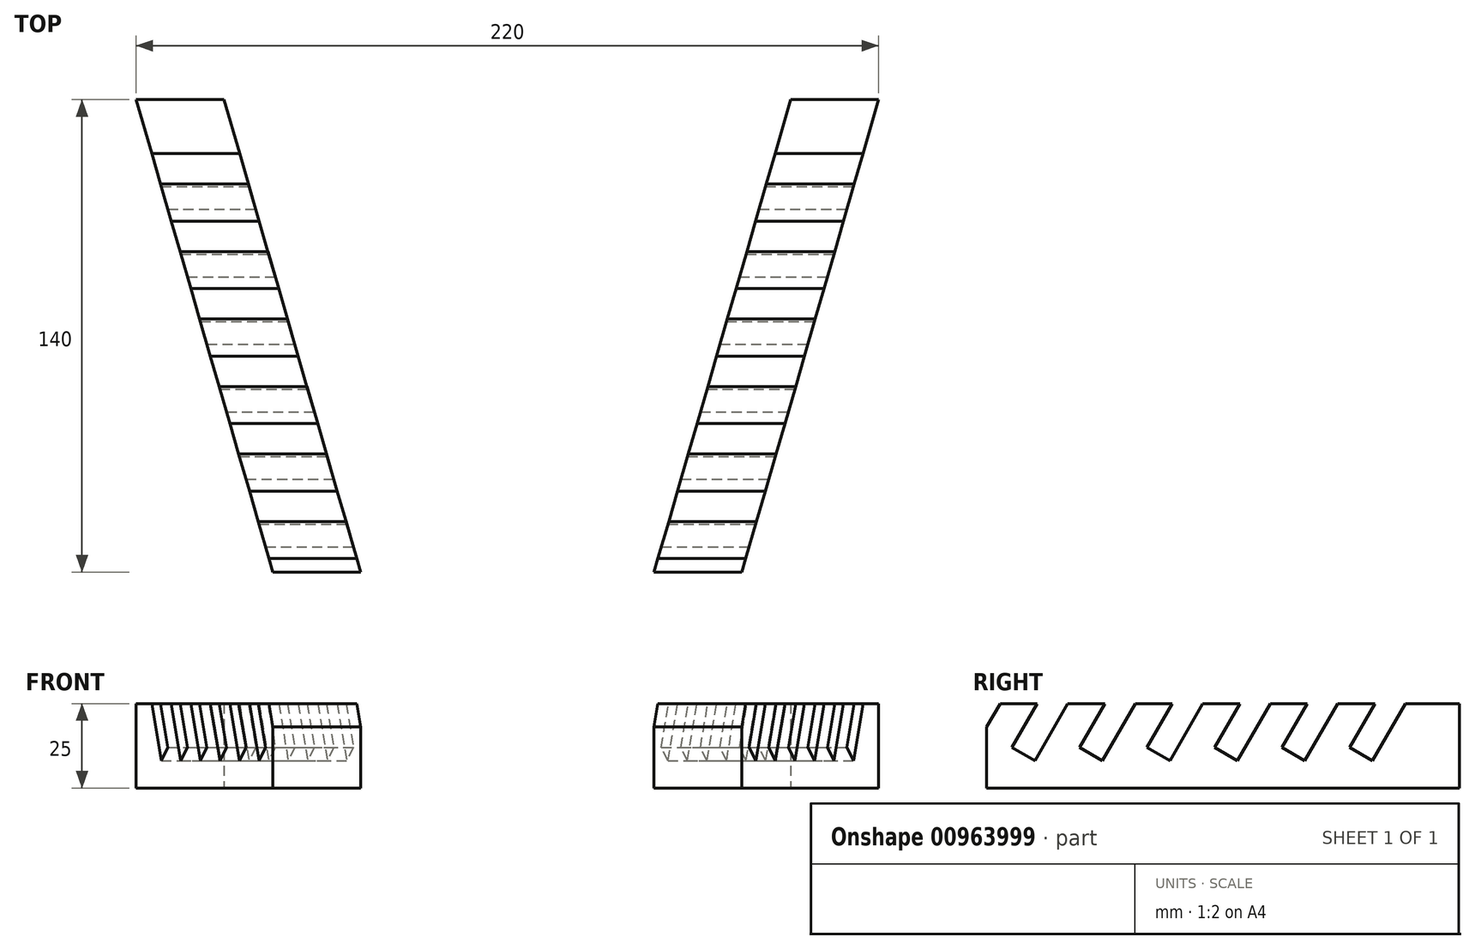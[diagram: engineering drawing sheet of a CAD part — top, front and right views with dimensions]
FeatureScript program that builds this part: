
annotation { "Feature Type Name" : "Feature", "Feature Type Description" : "" }
export const myFeature = defineFeature(function(context is Context, id is Id, definition is map)
    precondition{}
    {
        {
            var Q0;
            Q0=qCreatedBy(makeId("Top.planeOp"),FACE);
            var sketch = newSketch(context, id + "F0", { "sketchPlane" : qUnion([Q0])});
            skLineSegment(sketch, "E0", {"start": v(0, 0) * mm, "end": v(0, 380) * mm, "construction": true});
            skLineSegment(sketch, "E1", {"start": v(-110, 380) * mm, "end": v(-83.97, 380) * mm});
            skLineSegment(sketch, "E2", {"start": v(-110, 380) * mm, "end": v(0, 0) * mm});
            skLineSegment(sketch, "E3", {"start": v(110, 380) * mm, "end": v(0, 0) * mm});
            skLineSegment(sketch, "E4.0", {"start": v(-76.74, 355) * mm, "end": v(0, 89.9) * mm});
            skLineSegment(sketch, "E4.2", {"start": v(76.74, 355) * mm, "end": v(0, 89.9) * mm});
            skLineSegment(sketch, "E5", {"start": v(-76.74, 355) * mm, "end": v(-83.97, 380) * mm});
            skLineSegment(sketch, "E6", {"start": v(76.74, 355) * mm, "end": v(83.97, 380) * mm});
            skLineSegment(sketch, "E7.trimOffspring", {"start": v(83.97, 380) * mm, "end": v(110, 380) * mm});
            skSolve(sketch);
        }
        {
            var Q0;
            Q0=makeQuery(id+"F0.imprint","IMPRINT",FACE,{"disambiguationData":[TD([[makeQuery(id+"F0.imprint","IMPRINT",EDGE,{"derivedFrom":sQuery(id+"F0.wireOp",EDGE,"E1")}),-1.0]])]});
            extrude(context, id + "F1", {"entities" : qUnion([Q0]), "depth" : 25 * mm, "offsetDistance" : 25 * mm});
        }
        {
            var Q0;
            Q0=qCreatedBy(makeId("Right.planeOp"),FACE);
            var sketch = newSketch(context, id + "F2", { "sketchPlane" : qUnion([Q0])});
            skLineSegment(sketch, "E8", {"start": v(0, 0) * mm, "end": v(380, 0) * mm, "construction": true});
            skLineSegment(sketch, "E9", {"start": v(15, 0) * mm, "end": v(15, 35) * mm, "construction": true});
            skLineSegment(sketch, "E10", {"start": v(24, 0) * mm, "end": v(24, 35) * mm, "construction": true});
            skLineSegment(sketch, "E11", {"start": v(35, 0) * mm, "end": v(35, 35) * mm, "construction": true});
            skLineSegment(sketch, "E12", {"start": v(44, 0) * mm, "end": v(44, 35) * mm, "construction": true});
            skLineSegment(sketch, "E13", {"start": v(0, 0) * mm, "end": v(0, 25) * mm, "construction": true});
            skLineSegment(sketch, "E14", {"start": v(45.46, -18.54) * mm, "end": v(100.8, -18.54) * mm, "construction": true});
            skLineSegment(sketch, "E15", {"start": v(15, 25) * mm, "end": v(7.5, 12) * mm});
            skLineSegment(sketch, "E16", {"start": v(7.5, 12) * mm, "end": v(14.25, 8.11) * mm});
            skLineSegment(sketch, "E17", {"start": v(24, 25) * mm, "end": v(14.25, 8.11) * mm});
            skLineSegment(sketch, "E18", {"start": v(35, 25) * mm, "end": v(27.5, 12.01) * mm});
            skLineSegment(sketch, "E19", {"start": v(27.5, 12.01) * mm, "end": v(34.25, 8.11) * mm});
            skLineSegment(sketch, "E20", {"start": v(44, 25) * mm, "end": v(34.25, 8.11) * mm});
            skLineSegment(sketch, "E21", {"start": v(15, 25) * mm, "end": v(24, 25) * mm});
            skLineSegment(sketch, "E22", {"start": v(35, 25) * mm, "end": v(44, 25) * mm});
            skLineSegment(sketch, "E23", {"start": v(55, 25) * mm, "end": v(47.5, 12) * mm});
            skLineSegment(sketch, "E24", {"start": v(47.5, 12) * mm, "end": v(54.25, 8.11) * mm});
            skLineSegment(sketch, "E25", {"start": v(64, 25) * mm, "end": v(54.25, 8.11) * mm});
            skLineSegment(sketch, "E26", {"start": v(75, 25) * mm, "end": v(67.5, 12.01) * mm});
            skLineSegment(sketch, "E27", {"start": v(67.5, 12.01) * mm, "end": v(74.25, 8.11) * mm});
            skLineSegment(sketch, "E28", {"start": v(84, 25) * mm, "end": v(74.25, 8.11) * mm});
            skLineSegment(sketch, "E29", {"start": v(55, 25) * mm, "end": v(64, 25) * mm});
            skLineSegment(sketch, "E30", {"start": v(75, 25) * mm, "end": v(84, 25) * mm});
            skLineSegment(sketch, "E31", {"start": v(95, 25) * mm, "end": v(87.5, 12.01) * mm});
            skLineSegment(sketch, "E32", {"start": v(87.5, 12.01) * mm, "end": v(94.25, 8.11) * mm});
            skLineSegment(sketch, "E33", {"start": v(104, 25) * mm, "end": v(94.25, 8.11) * mm});
            skLineSegment(sketch, "E34", {"start": v(115, 25) * mm, "end": v(107.5, 12.01) * mm});
            skLineSegment(sketch, "E35", {"start": v(107.5, 12.01) * mm, "end": v(114.25, 8.11) * mm});
            skLineSegment(sketch, "E36", {"start": v(124, 25) * mm, "end": v(114.25, 8.11) * mm});
            skLineSegment(sketch, "E37", {"start": v(95, 25) * mm, "end": v(104, 25) * mm});
            skLineSegment(sketch, "E38", {"start": v(115, 25) * mm, "end": v(124, 25) * mm});
            skLineSegment(sketch, "E39", {"start": v(135, 25) * mm, "end": v(127.5, 12.01) * mm});
            skLineSegment(sketch, "E40", {"start": v(127.5, 12.01) * mm, "end": v(134.25, 8.11) * mm});
            skLineSegment(sketch, "E41", {"start": v(144, 25) * mm, "end": v(134.25, 8.11) * mm});
            skLineSegment(sketch, "E42", {"start": v(155, 25) * mm, "end": v(147.5, 12.01) * mm});
            skLineSegment(sketch, "E43", {"start": v(147.5, 12.01) * mm, "end": v(154.25, 8.11) * mm});
            skLineSegment(sketch, "E44", {"start": v(164, 25) * mm, "end": v(154.25, 8.11) * mm});
            skLineSegment(sketch, "E45", {"start": v(135, 25) * mm, "end": v(144, 25) * mm});
            skLineSegment(sketch, "E46", {"start": v(155, 25) * mm, "end": v(164, 25) * mm});
            skLineSegment(sketch, "E47", {"start": v(175, 25) * mm, "end": v(167.5, 12.01) * mm});
            skLineSegment(sketch, "E48", {"start": v(167.5, 12.01) * mm, "end": v(174.25, 8.11) * mm});
            skLineSegment(sketch, "E49", {"start": v(184, 25) * mm, "end": v(174.25, 8.11) * mm});
            skLineSegment(sketch, "E50", {"start": v(195, 25) * mm, "end": v(187.5, 12.01) * mm});
            skLineSegment(sketch, "E51", {"start": v(187.5, 12.01) * mm, "end": v(194.25, 8.11) * mm});
            skLineSegment(sketch, "E52", {"start": v(204, 25) * mm, "end": v(194.25, 8.11) * mm});
            skLineSegment(sketch, "E53", {"start": v(175, 25) * mm, "end": v(184, 25) * mm});
            skLineSegment(sketch, "E54", {"start": v(195, 25) * mm, "end": v(204, 25) * mm});
            skLineSegment(sketch, "E55", {"start": v(215, 25) * mm, "end": v(207.5, 12.01) * mm});
            skLineSegment(sketch, "E56", {"start": v(207.5, 12.01) * mm, "end": v(214.25, 8.11) * mm});
            skLineSegment(sketch, "E57", {"start": v(224, 25) * mm, "end": v(214.25, 8.11) * mm});
            skLineSegment(sketch, "E58", {"start": v(235, 25) * mm, "end": v(227.5, 12.01) * mm});
            skLineSegment(sketch, "E59", {"start": v(227.5, 12.01) * mm, "end": v(234.25, 8.11) * mm});
            skLineSegment(sketch, "E60", {"start": v(244, 25) * mm, "end": v(234.25, 8.11) * mm});
            skLineSegment(sketch, "E61", {"start": v(215, 25) * mm, "end": v(224, 25) * mm});
            skLineSegment(sketch, "E62", {"start": v(235, 25) * mm, "end": v(244, 25) * mm});
            skLineSegment(sketch, "E63", {"start": v(255, 25) * mm, "end": v(247.5, 12.01) * mm});
            skLineSegment(sketch, "E64", {"start": v(247.5, 12.01) * mm, "end": v(254.25, 8.11) * mm});
            skLineSegment(sketch, "E65", {"start": v(264, 25) * mm, "end": v(254.25, 8.11) * mm});
            skLineSegment(sketch, "E66", {"start": v(275, 25) * mm, "end": v(267.5, 12.01) * mm});
            skLineSegment(sketch, "E67", {"start": v(267.5, 12.01) * mm, "end": v(274.25, 8.11) * mm});
            skLineSegment(sketch, "E68", {"start": v(284, 25) * mm, "end": v(274.25, 8.11) * mm});
            skLineSegment(sketch, "E69", {"start": v(255, 25) * mm, "end": v(264, 25) * mm});
            skLineSegment(sketch, "E70", {"start": v(275, 25) * mm, "end": v(284, 25) * mm});
            skLineSegment(sketch, "E71", {"start": v(295, 25) * mm, "end": v(287.5, 12.01) * mm});
            skLineSegment(sketch, "E72", {"start": v(287.5, 12.01) * mm, "end": v(294.25, 8.12) * mm});
            skLineSegment(sketch, "E73", {"start": v(304, 25) * mm, "end": v(294.25, 8.12) * mm});
            skLineSegment(sketch, "E74", {"start": v(295, 25) * mm, "end": v(304, 25) * mm});
            skLineSegment(sketch, "E75", {"start": v(315, 25) * mm, "end": v(307.5, 12.01) * mm});
            skLineSegment(sketch, "E76", {"start": v(307.5, 12.01) * mm, "end": v(314.25, 8.11) * mm});
            skLineSegment(sketch, "E77", {"start": v(324, 25) * mm, "end": v(314.25, 8.11) * mm});
            skLineSegment(sketch, "E78", {"start": v(335, 25) * mm, "end": v(327.5, 12.01) * mm});
            skLineSegment(sketch, "E79", {"start": v(327.5, 12.01) * mm, "end": v(334.25, 8.12) * mm});
            skLineSegment(sketch, "E80", {"start": v(344, 25) * mm, "end": v(334.25, 8.12) * mm});
            skLineSegment(sketch, "E81", {"start": v(315, 25) * mm, "end": v(324, 25) * mm});
            skLineSegment(sketch, "E82", {"start": v(335, 25) * mm, "end": v(344, 25) * mm});
            skLineSegment(sketch, "E83", {"start": v(355, 25) * mm, "end": v(347.5, 12.01) * mm});
            skLineSegment(sketch, "E84", {"start": v(347.5, 12.01) * mm, "end": v(354.25, 8.12) * mm});
            skLineSegment(sketch, "E85", {"start": v(364, 25) * mm, "end": v(354.25, 8.12) * mm});
            skLineSegment(sketch, "E86", {"start": v(355, 25) * mm, "end": v(364, 25) * mm});
            skLineSegment(sketch, "E87", {"start": v(0, 25) * mm, "end": v(0, 95.98) * mm, "construction": true});
            skLineSegment(sketch, "E88", {"start": v(0, 95.98) * mm, "end": v(380, 95.98) * mm, "construction": true});
            skLineSegment(sketch, "E89", {"start": v(120, 105.15) * mm, "end": v(120, 75.15) * mm, "construction": true});
            skLineSegment(sketch, "E90", {"start": v(380, 109.48) * mm, "end": v(380, 79.48) * mm, "construction": true});
            skLineSegment(sketch, "E91", {"start": v(240, 110.66) * mm, "end": v(240, 80.66) * mm, "construction": true});
            skSolve(sketch);
        }
        {
            var Q0;
            Q0 = qSketchRegion(id + "F2", true);
            extrude(context, id + "F3", {"entities" : qUnion([Q0]), "operationType" : NewBodyOperationType.REMOVE, "endBound" : BoundingType.SYMMETRIC, "oppositeDirection" : true, "depth" : 500 * mm, "offsetDistance" : 25 * mm});
        }
        {
            var Q0;
            Q0=sQuery(id+"F2.wireOp",EDGE,"E89");
            cPlane(context, id + "F4", {"entities" : qUnion([Q0]), "cplaneType" : CPlaneType.LINE_ANGLE, "offset" : 25 * mm, "angle" : 90 * degree, "width" : 150 * mm, "height" : 150 * mm});
        }
        {
            var Q0;
            Q0=sQuery(id+"F2.wireOp",EDGE,"E91");
            cPlane(context, id + "F5", {"entities" : qUnion([Q0]), "cplaneType" : CPlaneType.LINE_ANGLE, "offset" : 25 * mm, "angle" : 90 * degree, "width" : 150 * mm, "height" : 150 * mm});
        }
        {
            var Q0;
            Q0=qCreatedBy(id+"F4.planeOp",FACE);
            var sketch = newSketch(context, id + "F6", { "sketchPlane" : qUnion([Q0])});
            skLineSegment(sketch, "E92.bottom", {"start": v(185.94, 139.15) * mm, "end": v(-173.02, 139.15) * mm});
            skLineSegment(sketch, "E92.top", {"start": v(185.94, -61.04) * mm, "end": v(-173.02, -61.04) * mm});
            skLineSegment(sketch, "E92.left", {"start": v(185.94, 139.15) * mm, "end": v(185.94, -61.04) * mm});
            skLineSegment(sketch, "E92.right", {"start": v(-173.02, 139.15) * mm, "end": v(-173.02, -61.04) * mm});
            skSolve(sketch);
        }
        {
            var Q0;
            Q0=makeQuery(id+"F6.imprint","IMPRINT",FACE,{"disambiguationData":[TD([[makeQuery(id+"F6.imprint","IMPRINT",EDGE,{"derivedFrom":sQuery(id+"F6.wireOp",EDGE,"E92.bottom")}),1.0]])]});
            extrude(context, id + "F7", {"entities" : qUnion([Q0]), "operationType" : NewBodyOperationType.REMOVE, "oppositeDirection" : true, "depth" : 379 * mm, "offsetDistance" : 25 * mm});
        }
        {
            var Q0;
            Q0=qCreatedBy(id+"F5.planeOp",FACE);
            var sketch = newSketch(context, id + "F8", { "sketchPlane" : qUnion([Q0])});
            skLineSegment(sketch, "E93.bottom", {"start": v(171.04, 132.43) * mm, "end": v(-183.25, 132.43) * mm});
            skLineSegment(sketch, "E93.top", {"start": v(171.04, -65.66) * mm, "end": v(-183.25, -65.66) * mm});
            skLineSegment(sketch, "E93.left", {"start": v(171.04, 132.43) * mm, "end": v(171.04, -65.66) * mm});
            skLineSegment(sketch, "E93.right", {"start": v(-183.25, 132.43) * mm, "end": v(-183.25, -65.66) * mm});
            skSolve(sketch);
        }
        {
            var Q0;
            Q0=makeQuery(id+"F8.imprint","IMPRINT",FACE,{"disambiguationData":[TD([[makeQuery(id+"F8.imprint","IMPRINT",EDGE,{"derivedFrom":sQuery(id+"F8.wireOp",EDGE,"E93.bottom")}),1.0]])]});
            extrude(context, id + "F9", {"entities" : qUnion([Q0]), "operationType" : NewBodyOperationType.REMOVE, "oppositeDirection" : true, "depth" : 158 * mm, "offsetDistance" : 25 * mm});
        }
    });
